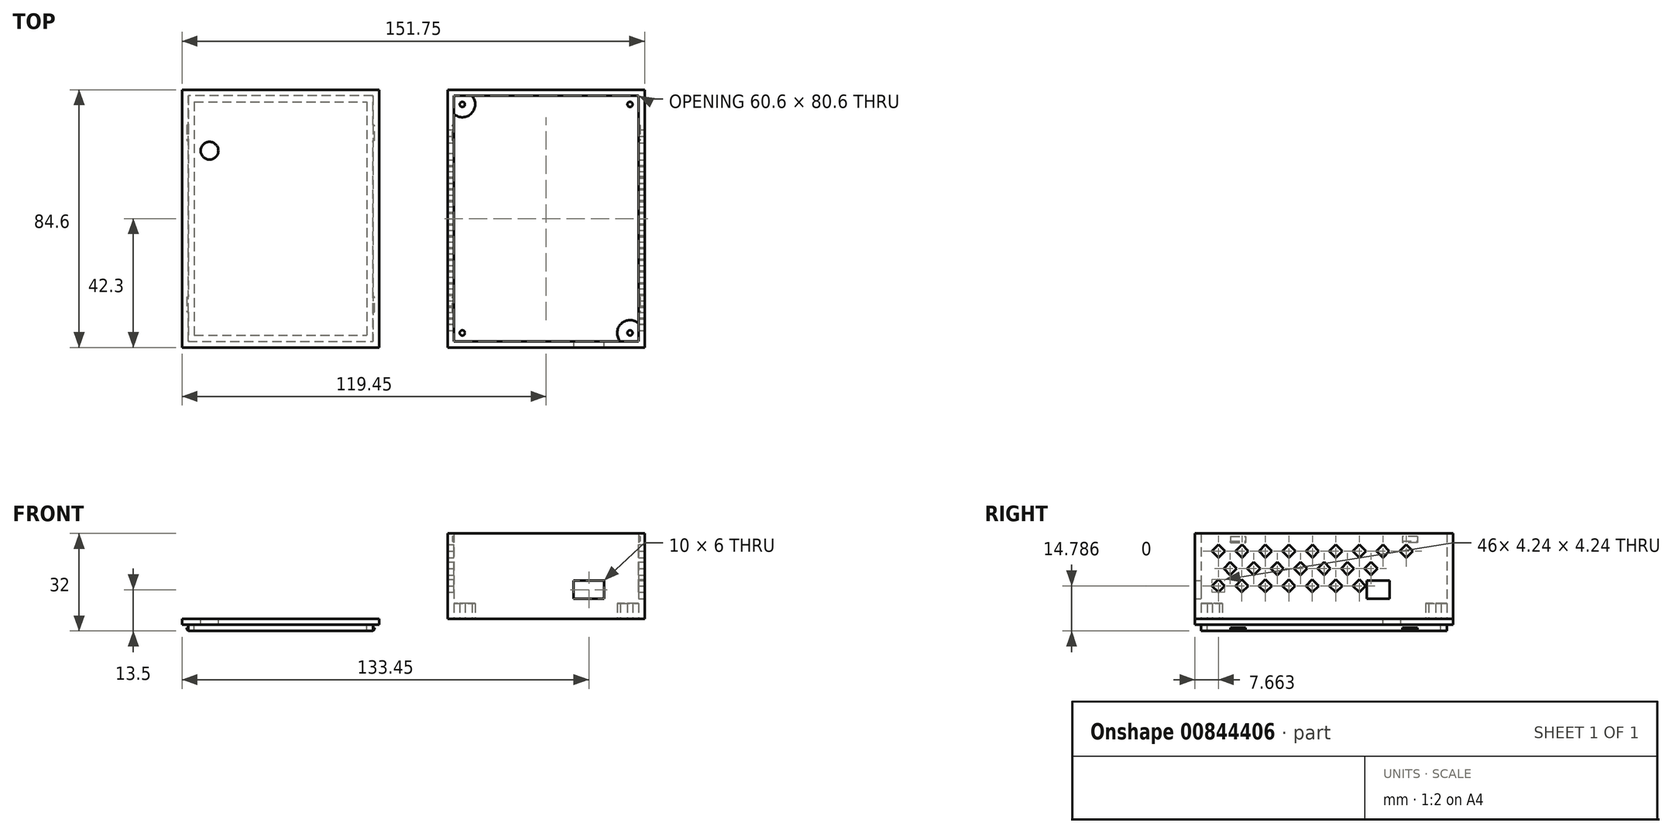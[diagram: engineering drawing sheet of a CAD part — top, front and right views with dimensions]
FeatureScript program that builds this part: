
annotation { "Feature Type Name" : "Feature", "Feature Type Description" : "" }
export const myFeature = defineFeature(function(context is Context, id is Id, definition is map)
    precondition{}
    {
        {
            var Q0;
            Q0=qCreatedBy(makeId("Top.planeOp"),FACE);
            var sketch = newSketch(context, id + "F0", { "sketchPlane" : qUnion([Q0])});
            skLineSegment(sketch, "E0", {"start": v(0, 47.12) * mm, "end": v(0, -56.68) * mm, "construction": true});
            skLineSegment(sketch, "E1", {"start": v(-53.86, 0) * mm, "end": v(97.7, 0) * mm, "construction": true});
            skCircle(sketch, "E2", {"center": v(-27.5, 37.5) * mm, "radius": 0.85 * mm});
            skLineSegment(sketch, "E3", {"start": v(-32.3, 0) * mm, "end": v(-32.3, 42.3) * mm});
            skLineSegment(sketch, "E4", {"start": v(-32.3, 42.3) * mm, "end": v(0, 42.3) * mm});
            skLineSegment(sketch, "E5", {"start": v(0, 40.3) * mm, "end": v(-30.3, 40.3) * mm});
            skLineSegment(sketch, "E6", {"start": v(-30.3, 40.3) * mm, "end": v(-30.3, 0) * mm});
            skCircle(sketch, "E7.MirrorC", {"center": v(27.5, 37.5) * mm, "radius": 0.85 * mm});
            skLineSegment(sketch, "E8.MirrorCS", {"start": v(32.3, 0) * mm, "end": v(32.3, 42.3) * mm});
            skLineSegment(sketch, "E9.MirrorCS", {"start": v(0, 40.3) * mm, "end": v(30.3, 40.3) * mm});
            skLineSegment(sketch, "E10.MirrorCS", {"start": v(30.3, 40.3) * mm, "end": v(30.3, 0) * mm});
            skLineSegment(sketch, "E11.MirrorCS", {"start": v(32.3, 42.3) * mm, "end": v(0, 42.3) * mm});
            skLineSegment(sketch, "E12.MirrorCS", {"start": v(-32.3, 0) * mm, "end": v(-32.3, -42.3) * mm});
            skLineSegment(sketch, "E13.MirrorCS", {"start": v(-30.3, -40.3) * mm, "end": v(-30.3, 0) * mm});
            skLineSegment(sketch, "E14.MirrorCS", {"start": v(30.3, -40.3) * mm, "end": v(30.3, 0) * mm});
            skLineSegment(sketch, "E15.MirrorCS", {"start": v(32.3, 0) * mm, "end": v(32.3, -42.3) * mm});
            skCircle(sketch, "E16.MirrorC", {"center": v(27.5, -37.5) * mm, "radius": 0.85 * mm});
            skCircle(sketch, "E17.MirrorC", {"center": v(-27.5, -37.5) * mm, "radius": 0.85 * mm});
            skLineSegment(sketch, "E18.MirrorCS", {"start": v(-32.3, -42.3) * mm, "end": v(0, -42.3) * mm});
            skLineSegment(sketch, "E19.MirrorCS", {"start": v(0, -40.3) * mm, "end": v(-30.3, -40.3) * mm});
            skLineSegment(sketch, "E20.MirrorCS", {"start": v(32.3, -42.3) * mm, "end": v(0, -42.3) * mm});
            skLineSegment(sketch, "E21.MirrorCS", {"start": v(0, -40.3) * mm, "end": v(30.3, -40.3) * mm});
            skLineSegment(sketch, "E22", {"start": v(30.3, 14) * mm, "end": v(32.3, 14) * mm});
            skLineSegment(sketch, "E23", {"start": v(30.3, 21.5) * mm, "end": v(32.3, 21.5) * mm});
            skLineSegment(sketch, "E24", {"start": v(19, -42.3) * mm, "end": v(19, -40.3) * mm});
            skLineSegment(sketch, "E25", {"start": v(9, -40.3) * mm, "end": v(9, -42.3) * mm});
            skArc(sketch, "E26", {"start": v(-24.36, 40.3) * mm, "mid": v(-24.53, 34.53) * mm, "end": v(-30.3, 34.36) * mm});
            skArc(sketch, "E27.MirrorCS", {"start": v(24.36, 40.3) * mm, "mid": v(24.53, 34.53) * mm, "end": v(30.3, 34.36) * mm});
            skArc(sketch, "E28.MirrorCS", {"start": v(24.36, -40.3) * mm, "mid": v(24.53, -34.53) * mm, "end": v(30.3, -34.36) * mm});
            skArc(sketch, "E29.MirrorCS", {"start": v(-24.36, -40.3) * mm, "mid": v(-24.53, -34.53) * mm, "end": v(-30.3, -34.36) * mm});
            skLineSegment(sketch, "E30", {"start": v(-30.3, 30.67) * mm, "end": v(-30.8, 30.67) * mm});
            skLineSegment(sketch, "E31", {"start": v(-30.8, 30.67) * mm, "end": v(-30.8, 25.67) * mm});
            skLineSegment(sketch, "E32", {"start": v(-30.8, 25.67) * mm, "end": v(-30.3, 25.67) * mm});
            skLineSegment(sketch, "E33.MirrorCS", {"start": v(30.8, 25.67) * mm, "end": v(30.3, 25.67) * mm});
            skLineSegment(sketch, "E34.MirrorCS", {"start": v(30.3, 30.67) * mm, "end": v(30.8, 30.67) * mm});
            skLineSegment(sketch, "E35.MirrorCS", {"start": v(30.8, 30.67) * mm, "end": v(30.8, 25.67) * mm});
            skLineSegment(sketch, "E36.MirrorCS", {"start": v(30.8, -25.67) * mm, "end": v(30.3, -25.67) * mm});
            skLineSegment(sketch, "E37.MirrorCS", {"start": v(30.3, -30.67) * mm, "end": v(30.8, -30.67) * mm});
            skLineSegment(sketch, "E38.MirrorCS", {"start": v(30.8, -30.67) * mm, "end": v(30.8, -25.67) * mm});
            skLineSegment(sketch, "E39.MirrorCS", {"start": v(-30.8, -25.67) * mm, "end": v(-30.3, -25.67) * mm});
            skLineSegment(sketch, "E40.MirrorCS", {"start": v(-30.8, -30.67) * mm, "end": v(-30.8, -25.67) * mm});
            skLineSegment(sketch, "E41.MirrorCS", {"start": v(-30.3, -30.67) * mm, "end": v(-30.8, -30.67) * mm});
            skLineSegment(sketch, "E42", {"start": v(-43.57, 67.12) * mm, "end": v(-43.57, -62.63) * mm, "construction": true});
            skLineSegment(sketch, "E43.MirrorCS", {"start": v(-56.85, 30.67) * mm, "end": v(-56.35, 30.67) * mm});
            skLineSegment(sketch, "E44.MirrorCS", {"start": v(-117.95, -25.67) * mm, "end": v(-117.45, -25.67) * mm});
            skLineSegment(sketch, "E45.MirrorCS", {"start": v(-117.45, -30.67) * mm, "end": v(-117.95, -30.67) * mm});
            skLineSegment(sketch, "E46.MirrorCS", {"start": v(-56.85, -30.67) * mm, "end": v(-56.35, -30.67) * mm});
            skLineSegment(sketch, "E47.MirrorCS", {"start": v(-117.95, 30.67) * mm, "end": v(-117.95, 25.67) * mm});
            skLineSegment(sketch, "E48.MirrorCS", {"start": v(-56.35, -25.67) * mm, "end": v(-56.85, -25.67) * mm});
            skLineSegment(sketch, "E49.MirrorCS", {"start": v(-117.45, 30.67) * mm, "end": v(-117.95, 30.67) * mm});
            skLineSegment(sketch, "E50.MirrorCS", {"start": v(-117.95, 25.67) * mm, "end": v(-117.45, 25.67) * mm});
            skLineSegment(sketch, "E51.MirrorCS", {"start": v(-56.35, 25.67) * mm, "end": v(-56.85, 25.67) * mm});
            skLineSegment(sketch, "E52.MirrorCS", {"start": v(-117.95, -30.67) * mm, "end": v(-117.95, -25.67) * mm});
            skLineSegment(sketch, "E53.MirrorCS", {"start": v(-56.35, 30.67) * mm, "end": v(-56.35, 25.67) * mm});
            skLineSegment(sketch, "E54.MirrorCS", {"start": v(-56.35, -30.67) * mm, "end": v(-56.35, -25.67) * mm});
            skLineSegment(sketch, "E55.MirrorCS", {"start": v(-119.45, 0) * mm, "end": v(-119.45, 42.3) * mm});
            skLineSegment(sketch, "E56.MirrorCS", {"start": v(-87.15, -40.3) * mm, "end": v(-56.85, -40.3) * mm});
            skLineSegment(sketch, "E57.MirrorCS", {"start": v(-117.45, 40.3) * mm, "end": v(-117.45, 0) * mm});
            skLineSegment(sketch, "E58.MirrorCS", {"start": v(-119.45, 0) * mm, "end": v(-119.45, -42.3) * mm});
            skLineSegment(sketch, "E59.MirrorCS", {"start": v(-87.15, 40.3) * mm, "end": v(-117.45, 40.3) * mm});
            skLineSegment(sketch, "E60.MirrorCS", {"start": v(-119.45, -42.3) * mm, "end": v(-87.15, -42.3) * mm});
            skLineSegment(sketch, "E61.MirrorCS", {"start": v(-54.85, 0) * mm, "end": v(-54.85, -42.3) * mm});
            skLineSegment(sketch, "E62.MirrorCS", {"start": v(-54.85, 42.3) * mm, "end": v(-87.15, 42.3) * mm});
            skLineSegment(sketch, "E63.MirrorCS", {"start": v(-56.85, 40.3) * mm, "end": v(-56.85, 0) * mm});
            skLineSegment(sketch, "E64.MirrorCS", {"start": v(-54.85, 0) * mm, "end": v(-54.85, 42.3) * mm});
            skLineSegment(sketch, "E65.MirrorCS", {"start": v(-56.85, -40.3) * mm, "end": v(-56.85, 0) * mm});
            skLineSegment(sketch, "E66.MirrorCS", {"start": v(-87.15, -40.3) * mm, "end": v(-117.45, -40.3) * mm});
            skLineSegment(sketch, "E67.MirrorCS", {"start": v(-87.15, 40.3) * mm, "end": v(-56.85, 40.3) * mm});
            skLineSegment(sketch, "E68.MirrorCS", {"start": v(-117.45, -40.3) * mm, "end": v(-117.45, 0) * mm});
            skLineSegment(sketch, "E69.MirrorCS", {"start": v(-54.85, -42.3) * mm, "end": v(-87.15, -42.3) * mm});
            skLineSegment(sketch, "E70.MirrorCS", {"start": v(-119.45, 42.3) * mm, "end": v(-87.15, 42.3) * mm});
            skLineSegment(sketch, "E71.bottom", {"start": v(-115.45, 38.3) * mm, "end": v(-58.85, 38.3) * mm});
            skLineSegment(sketch, "E71.top", {"start": v(-115.45, -38.3) * mm, "end": v(-58.85, -38.3) * mm});
            skLineSegment(sketch, "E71.left", {"start": v(-115.45, 38.3) * mm, "end": v(-115.45, -38.3) * mm});
            skLineSegment(sketch, "E71.right", {"start": v(-58.85, 38.3) * mm, "end": v(-58.85, -38.3) * mm});
            skCircle(sketch, "E72", {"center": v(-110.45, 22.3) * mm, "radius": 2.9 * mm});
            skSolve(sketch);
        }
        {
            var Q0;
            {var subQ7=sQuery(id+"F0.wireOp",EDGE,"E56.MirrorCS");Q0=makeQuery(id+"F0.imprint","IMPRINT",FACE,{"disambiguationData":[TD([[makeQuery(id+"F0.imprint","IMPRINT",EDGE,{"derivedFrom":subQ7}),1.0]])]});}
            extrude(context, id + "F1", {"entities" : qUnion([Q0]), "oppositeDirection" : true, "depth" : 4 * mm, "offsetDistance" : 25 * mm});
        }
        {
            var Q0;
            {var subQ1=sQuery(id+"F0.wireOp",EDGE,"E43.MirrorCS");Q0=makeQuery(id+"F0.imprint","IMPRINT",FACE,{"disambiguationData":[TD([[makeQuery(id+"F0.imprint","IMPRINT",EDGE,{"derivedFrom":subQ1}),1.0]])]});}
            var Q1;
            Q1=makeQuery(id+"F0.imprint","IMPRINT",FACE,{"disambiguationData":[TD([[makeQuery(id+"F0.imprint","IMPRINT",EDGE,{"derivedFrom":sQuery(id+"F0.wireOp",EDGE,"E71.bottom")}),-1.0]])]});
            var Q2;
            Q2=makeQuery(id+"F0.imprint","IMPRINT",FACE,{"disambiguationData":[TD([[makeQuery(id+"F0.imprint","IMPRINT",EDGE,{"derivedFrom":sQuery(id+"F0.wireOp",EDGE,"E47.MirrorCS")}),1.0]])]});
            var Q3;
            {var subQ0=sQuery(id+"F0.wireOp",EDGE,"E43.MirrorCS");Q3=makeQuery(id+"F0.imprint","IMPRINT",FACE,{"disambiguationData":[TD([[makeQuery(id+"F0.imprint","IMPRINT",EDGE,{"derivedFrom":subQ0}),-1.0]])]});}
            var Q4;
            {var subQ0=sQuery(id+"F0.wireOp",EDGE,"E46.MirrorCS");Q4=makeQuery(id+"F0.imprint","IMPRINT",FACE,{"disambiguationData":[TD([[makeQuery(id+"F0.imprint","IMPRINT",EDGE,{"derivedFrom":subQ0}),1.0]])]});}
            var Q5;
            {var subQ0=sQuery(id+"F0.wireOp",EDGE,"E44.MirrorCS");Q5=makeQuery(id+"F0.imprint","IMPRINT",FACE,{"disambiguationData":[TD([[makeQuery(id+"F0.imprint","IMPRINT",EDGE,{"derivedFrom":subQ0}),-1.0]])]});}
            extrude(context, id + "F2", {"entities" : qUnion([Q0, Q1, Q2, Q3, Q4, Q5]), "operationType" : NewBodyOperationType.ADD, "oppositeDirection" : true, "depth" : 2 * mm, "offsetDistance" : 25 * mm});
        }
        {
            var Q0;
            {var subQ0=sQuery(id+"F0.wireOp",EDGE,"E46.MirrorCS");Q0=makeQuery(id+"F0.imprint","IMPRINT",FACE,{"disambiguationData":[TD([[makeQuery(id+"F0.imprint","IMPRINT",EDGE,{"derivedFrom":subQ0}),1.0]])]});}
            var Q1;
            {var subQ0=sQuery(id+"F0.wireOp",EDGE,"E43.MirrorCS");Q1=makeQuery(id+"F0.imprint","IMPRINT",FACE,{"disambiguationData":[TD([[makeQuery(id+"F0.imprint","IMPRINT",EDGE,{"derivedFrom":subQ0}),-1.0]])]});}
            var Q2;
            Q2=makeQuery(id+"F0.imprint","IMPRINT",FACE,{"disambiguationData":[TD([[makeQuery(id+"F0.imprint","IMPRINT",EDGE,{"derivedFrom":sQuery(id+"F0.wireOp",EDGE,"E47.MirrorCS")}),1.0]])]});
            var Q3;
            {var subQ0=sQuery(id+"F0.wireOp",EDGE,"E44.MirrorCS");Q3=makeQuery(id+"F0.imprint","IMPRINT",FACE,{"disambiguationData":[TD([[makeQuery(id+"F0.imprint","IMPRINT",EDGE,{"derivedFrom":subQ0}),-1.0]])]});}
            extrude(context, id + "F3", {"entities" : qUnion([Q0, Q1, Q2, Q3]), "operationType" : NewBodyOperationType.ADD, "oppositeDirection" : true, "depth" : 4 * mm, "offsetDistance" : 25 * mm, "hasSecondDirection" : true, "secondDirectionOppositeDirection" : true, "secondDirectionDepth" : 3 * mm});
        }
        {
            var Q0;
            Q0=makeQuery(id+"F0.imprint","IMPRINT",FACE,{"disambiguationData":[TD([[makeQuery(id+"F0.imprint","IMPRINT",EDGE,{"derivedFrom":sQuery(id+"F0.wireOp",EDGE,"E2")}),-1.0]])]});
            var Q1;
            Q1=makeQuery(id+"F0.imprint","IMPRINT",FACE,{"disambiguationData":[TD([[makeQuery(id+"F0.imprint","IMPRINT",EDGE,{"derivedFrom":sQuery(id+"F0.wireOp",EDGE,"E7.MirrorC")}),1.0]])]});
            var Q2;
            Q2=makeQuery(id+"F0.imprint","IMPRINT",FACE,{"disambiguationData":[TD([[makeQuery(id+"F0.imprint","IMPRINT",EDGE,{"derivedFrom":sQuery(id+"F0.wireOp",EDGE,"E16.MirrorC")}),-1.0]])]});
            var Q3;
            Q3=makeQuery(id+"F0.imprint","IMPRINT",FACE,{"disambiguationData":[TD([[makeQuery(id+"F0.imprint","IMPRINT",EDGE,{"derivedFrom":sQuery(id+"F0.wireOp",EDGE,"E17.MirrorC")}),1.0]])]});
            extrude(context, id + "F4", {"entities" : qUnion([Q0, Q1, Q2, Q3]), "depth" : 5 * mm, "offsetDistance" : 25 * mm});
        }
        {
            var Q0;
            {var subQ7=sQuery(id+"F0.wireOp",EDGE,"E26");Q0=makeQuery(id+"F0.imprint","IMPRINT",FACE,{"disambiguationData":[TD([[makeQuery(id+"F0.imprint","IMPRINT",EDGE,{"derivedFrom":subQ7}),1.0]])]});}
            extrude(context, id + "F5", {"entities" : qUnion([Q0]), "operationType" : NewBodyOperationType.ADD, "depth" : 2 * mm, "offsetDistance" : 25 * mm});
        }
        {
            var Q0;
            {var subQ0=sQuery(id+"F0.wireOp",EDGE,"E36.MirrorCS");Q0=makeQuery(id+"F0.imprint","IMPRINT",FACE,{"disambiguationData":[TD([[makeQuery(id+"F0.imprint","IMPRINT",EDGE,{"derivedFrom":subQ0}),1.0]])]});}
            var Q1;
            {var subQ2=sQuery(id+"F0.wireOp",EDGE,"E15.MirrorCS");Q1=makeQuery(id+"F0.imprint","IMPRINT",FACE,{"disambiguationData":[TD([[makeQuery(id+"F0.imprint","IMPRINT",EDGE,{"derivedFrom":subQ2}),-1.0]])]});}
            var Q2;
            {var subQ0=sQuery(id+"F0.wireOp",EDGE,"E24");Q2=makeQuery(id+"F0.imprint","IMPRINT",FACE,{"disambiguationData":[TD([[makeQuery(id+"F0.imprint","IMPRINT",EDGE,{"derivedFrom":subQ0}),1.0]])]});}
            var Q3;
            Q3=makeQuery(id+"F0.imprint","IMPRINT",FACE,{"disambiguationData":[TD([[makeQuery(id+"F0.imprint","IMPRINT",EDGE,{"derivedFrom":sQuery(id+"F0.wireOp",EDGE,"E3")}),-1.0]])]});
            var Q4;
            {var subQ0=sQuery(id+"F0.wireOp",EDGE,"E22");Q4=makeQuery(id+"F0.imprint","IMPRINT",FACE,{"disambiguationData":[TD([[makeQuery(id+"F0.imprint","IMPRINT",EDGE,{"derivedFrom":subQ0}),1.0]])]});}
            var Q5;
            {var subQ0=sQuery(id+"F0.wireOp",EDGE,"E33.MirrorCS");Q5=makeQuery(id+"F0.imprint","IMPRINT",FACE,{"disambiguationData":[TD([[makeQuery(id+"F0.imprint","IMPRINT",EDGE,{"derivedFrom":subQ0}),-1.0]])]});}
            var Q6;
            {var subQ0=sQuery(id+"F0.wireOp",EDGE,"E39.MirrorCS");Q6=makeQuery(id+"F0.imprint","IMPRINT",FACE,{"disambiguationData":[TD([[makeQuery(id+"F0.imprint","IMPRINT",EDGE,{"derivedFrom":subQ0}),-1.0]])]});}
            var Q7;
            {var subQ0=sQuery(id+"F0.wireOp",EDGE,"E30");Q7=makeQuery(id+"F0.imprint","IMPRINT",FACE,{"disambiguationData":[TD([[makeQuery(id+"F0.imprint","IMPRINT",EDGE,{"derivedFrom":subQ0}),1.0]])]});}
            extrude(context, id + "F6", {"entities" : qUnion([Q0, Q1, Q2, Q3, Q4, Q5, Q6, Q7]), "operationType" : NewBodyOperationType.ADD, "depth" : 28 * mm, "offsetDistance" : 25 * mm});
        }
        {
            var Q0;
            {var subQ0=sQuery(id+"F0.wireOp",EDGE,"E30");Q0=makeQuery(id+"F0.imprint","IMPRINT",FACE,{"disambiguationData":[TD([[makeQuery(id+"F0.imprint","IMPRINT",EDGE,{"derivedFrom":subQ0}),1.0]])]});}
            var Q1;
            {var subQ0=sQuery(id+"F0.wireOp",EDGE,"E39.MirrorCS");Q1=makeQuery(id+"F0.imprint","IMPRINT",FACE,{"disambiguationData":[TD([[makeQuery(id+"F0.imprint","IMPRINT",EDGE,{"derivedFrom":subQ0}),-1.0]])]});}
            var Q2;
            {var subQ0=sQuery(id+"F0.wireOp",EDGE,"E36.MirrorCS");Q2=makeQuery(id+"F0.imprint","IMPRINT",FACE,{"disambiguationData":[TD([[makeQuery(id+"F0.imprint","IMPRINT",EDGE,{"derivedFrom":subQ0}),1.0]])]});}
            var Q3;
            {var subQ0=sQuery(id+"F0.wireOp",EDGE,"E33.MirrorCS");Q3=makeQuery(id+"F0.imprint","IMPRINT",FACE,{"disambiguationData":[TD([[makeQuery(id+"F0.imprint","IMPRINT",EDGE,{"derivedFrom":subQ0}),-1.0]])]});}
            extrude(context, id + "F7", {"entities" : qUnion([Q0, Q1, Q2, Q3]), "operationType" : NewBodyOperationType.REMOVE, "depth" : 27 * mm, "offsetDistance" : 25 * mm, "hasSecondDirection" : true, "secondDirectionOppositeDirection" : false, "secondDirectionDepth" : 25 * mm});
        }
        {
            var Q0;
            Q0=makeQuery(id+"F7.boolean.opBoolean","COPY",EDGE,{"derivedFrom":makeQuery(id+"F7.opExtrude","CAP_EDGE",EDGE,{"disambiguationData":[OSD([sQuery(id+"F0.wireOp",EDGE,"E31")])],"isStart":true})});
            var Q1;
            Q1=makeQuery(id+"F7.boolean.opBoolean","COPY",EDGE,{"derivedFrom":makeQuery(id+"F7.opExtrude","CAP_EDGE",EDGE,{"disambiguationData":[OSD([sQuery(id+"F0.wireOp",EDGE,"E6")])],"isStart":false})});
            var Q2;
            Q2=makeQuery(id+"F7.boolean.opBoolean","COPY",EDGE,{"derivedFrom":makeQuery(id+"F7.opExtrude","CAP_EDGE",EDGE,{"disambiguationData":[OSD([sQuery(id+"F0.wireOp",EDGE,"E13.MirrorCS")])],"isStart":false})});
            var Q3;
            Q3=makeQuery(id+"F7.boolean.opBoolean","COPY",EDGE,{"derivedFrom":makeQuery(id+"F7.opExtrude","CAP_EDGE",EDGE,{"disambiguationData":[OSD([sQuery(id+"F0.wireOp",EDGE,"E40.MirrorCS")])],"isStart":true})});
            var Q4;
            Q4=makeQuery(id+"F7.boolean.opBoolean","COPY",EDGE,{"derivedFrom":makeQuery(id+"F7.opExtrude","CAP_EDGE",EDGE,{"disambiguationData":[OSD([sQuery(id+"F0.wireOp",EDGE,"E10.MirrorCS")])],"isStart":false})});
            var Q5;
            Q5=makeQuery(id+"F7.boolean.opBoolean","COPY",EDGE,{"derivedFrom":makeQuery(id+"F7.opExtrude","CAP_EDGE",EDGE,{"disambiguationData":[OSD([sQuery(id+"F0.wireOp",EDGE,"E35.MirrorCS")])],"isStart":true})});
            var Q6;
            Q6=makeQuery(id+"F7.boolean.opBoolean","COPY",EDGE,{"derivedFrom":makeQuery(id+"F7.opExtrude","CAP_EDGE",EDGE,{"disambiguationData":[OSD([sQuery(id+"F0.wireOp",EDGE,"E14.MirrorCS")])],"isStart":false})});
            var Q7;
            Q7=makeQuery(id+"F7.boolean.opBoolean","COPY",EDGE,{"derivedFrom":makeQuery(id+"F7.opExtrude","CAP_EDGE",EDGE,{"disambiguationData":[OSD([sQuery(id+"F0.wireOp",EDGE,"E38.MirrorCS")])],"isStart":true})});
            var Q8;
            Q8=makeQuery(id+"F3.opExtrude","CAP_EDGE",EDGE,{"disambiguationData":[OSD([sQuery(id+"F0.wireOp",EDGE,"E68.MirrorCS")])],"isStart":true});
            var Q9;
            Q9=makeQuery(id+"F3.opExtrude","CAP_EDGE",EDGE,{"disambiguationData":[OSD([sQuery(id+"F0.wireOp",EDGE,"E52.MirrorCS")])],"isStart":false});
            var Q10;
            Q10=makeQuery(id+"F3.opExtrude","CAP_EDGE",EDGE,{"disambiguationData":[OSD([sQuery(id+"F0.wireOp",EDGE,"E47.MirrorCS")])],"isStart":false});
            var Q11;
            Q11=makeQuery(id+"F3.opExtrude","CAP_EDGE",EDGE,{"disambiguationData":[OSD([sQuery(id+"F0.wireOp",EDGE,"E57.MirrorCS")])],"isStart":true});
            var Q12;
            Q12=makeQuery(id+"F3.opExtrude","CAP_EDGE",EDGE,{"disambiguationData":[OSD([sQuery(id+"F0.wireOp",EDGE,"E53.MirrorCS")])],"isStart":false});
            var Q13;
            Q13=makeQuery(id+"F3.opExtrude","CAP_EDGE",EDGE,{"disambiguationData":[OSD([sQuery(id+"F0.wireOp",EDGE,"E63.MirrorCS")])],"isStart":true});
            var Q14;
            Q14=makeQuery(id+"F3.opExtrude","CAP_EDGE",EDGE,{"disambiguationData":[OSD([sQuery(id+"F0.wireOp",EDGE,"E65.MirrorCS")])],"isStart":true});
            var Q15;
            Q15=makeQuery(id+"F3.opExtrude","CAP_EDGE",EDGE,{"disambiguationData":[OSD([sQuery(id+"F0.wireOp",EDGE,"E54.MirrorCS")])],"isStart":false});
            chamfer(context, id + "F8", {"entities" : qUnion([Q0, Q1, Q2, Q3, Q4, Q5, Q6, Q7, Q8, Q9, Q10, Q11, Q12, Q13, Q14, Q15]), "width" : 0.5 * mm, "tangentPropagation" : true});
        }
        {
            var Q0;
            {var subQ0=sQuery(id+"F0.wireOp",EDGE,"E24");Q0=makeQuery(id+"F0.imprint","IMPRINT",FACE,{"disambiguationData":[TD([[makeQuery(id+"F0.imprint","IMPRINT",EDGE,{"derivedFrom":subQ0}),1.0]])]});}
            var Q1;
            {var subQ0=sQuery(id+"F0.wireOp",EDGE,"E22");Q1=makeQuery(id+"F0.imprint","IMPRINT",FACE,{"disambiguationData":[TD([[makeQuery(id+"F0.imprint","IMPRINT",EDGE,{"derivedFrom":subQ0}),1.0]])]});}
            extrude(context, id + "F9", {"entities" : qUnion([Q0, Q1]), "operationType" : NewBodyOperationType.REMOVE, "depth" : 12.5 * mm, "offsetDistance" : 25 * mm, "hasSecondDirection" : true, "secondDirectionOppositeDirection" : false, "secondDirectionDepth" : 6.5 * mm});
        }
        {
            var Q0;
            Q0=makeQuery(id+"F6.opExtrude","SWEPT_FACE",FACE,{"disambiguationData":[OSD([sQuery(id+"F0.wireOp",EDGE,"E8.MirrorCS"),sQuery(id+"F0.wireOp",EDGE,"E15.MirrorCS")])]});
            var sketch = newSketch(context, id + "F10", { "sketchPlane" : qUnion([Q0])});
            skLineSegment(sketch, "E73.bottom", {"start": v(-42.3, 24.3) * mm, "end": v(-44.42, 22.19) * mm});
            skLineSegment(sketch, "E73.top", {"start": v(-40.18, 22.19) * mm, "end": v(-42.3, 20.07) * mm});
            skLineSegment(sketch, "E73.left", {"start": v(-42.3, 24.3) * mm, "end": v(-40.18, 22.19) * mm});
            skLineSegment(sketch, "E73.right", {"start": v(-44.42, 22.19) * mm, "end": v(-42.3, 20.07) * mm});
            skPoint(sketch, "E73.middle", {"position": v(-42.3, 22.19) * mm});
            skPoint(sketch, "E74.1.0.0", {"position": v(-34.6, 22.19) * mm});
            skLineSegment(sketch, "E74.1.0.1", {"start": v(-32.48, 22.19) * mm, "end": v(-34.6, 20.07) * mm});
            skLineSegment(sketch, "E74.1.0.2", {"start": v(-34.6, 24.3) * mm, "end": v(-32.48, 22.19) * mm});
            skLineSegment(sketch, "E74.1.0.3", {"start": v(-34.6, 24.3) * mm, "end": v(-36.72, 22.19) * mm});
            skLineSegment(sketch, "E74.1.0.4", {"start": v(-36.72, 22.19) * mm, "end": v(-34.6, 20.07) * mm});
            skPoint(sketch, "E74.2.0.0", {"position": v(-26.9, 22.19) * mm});
            skLineSegment(sketch, "E74.2.0.1", {"start": v(-24.78, 22.19) * mm, "end": v(-26.9, 20.07) * mm});
            skLineSegment(sketch, "E74.2.0.2", {"start": v(-26.9, 24.3) * mm, "end": v(-24.78, 22.19) * mm});
            skLineSegment(sketch, "E74.2.0.3", {"start": v(-26.9, 24.3) * mm, "end": v(-29.02, 22.19) * mm});
            skLineSegment(sketch, "E74.2.0.4", {"start": v(-29.02, 22.19) * mm, "end": v(-26.9, 20.07) * mm});
            skPoint(sketch, "E74.3.0.0", {"position": v(-19.2, 22.19) * mm});
            skLineSegment(sketch, "E74.3.0.1", {"start": v(-17.08, 22.19) * mm, "end": v(-19.2, 20.07) * mm});
            skLineSegment(sketch, "E74.3.0.2", {"start": v(-19.2, 24.3) * mm, "end": v(-17.08, 22.19) * mm});
            skLineSegment(sketch, "E74.3.0.3", {"start": v(-19.2, 24.3) * mm, "end": v(-21.32, 22.19) * mm});
            skLineSegment(sketch, "E74.3.0.4", {"start": v(-21.32, 22.19) * mm, "end": v(-19.2, 20.07) * mm});
            skPoint(sketch, "E74.4.0.0", {"position": v(-11.5, 22.19) * mm});
            skLineSegment(sketch, "E74.4.0.1", {"start": v(-9.38, 22.19) * mm, "end": v(-11.5, 20.07) * mm});
            skLineSegment(sketch, "E74.4.0.2", {"start": v(-11.5, 24.3) * mm, "end": v(-9.38, 22.19) * mm});
            skLineSegment(sketch, "E74.4.0.3", {"start": v(-11.5, 24.3) * mm, "end": v(-13.62, 22.19) * mm});
            skLineSegment(sketch, "E74.4.0.4", {"start": v(-13.62, 22.19) * mm, "end": v(-11.5, 20.07) * mm});
            skPoint(sketch, "E74.5.0.0", {"position": v(-3.8, 22.19) * mm});
            skLineSegment(sketch, "E74.5.0.1", {"start": v(-1.68, 22.19) * mm, "end": v(-3.8, 20.07) * mm});
            skLineSegment(sketch, "E74.5.0.2", {"start": v(-3.8, 24.3) * mm, "end": v(-1.68, 22.19) * mm});
            skLineSegment(sketch, "E74.5.0.3", {"start": v(-3.8, 24.3) * mm, "end": v(-5.92, 22.19) * mm});
            skLineSegment(sketch, "E74.5.0.4", {"start": v(-5.92, 22.19) * mm, "end": v(-3.8, 20.07) * mm});
            skPoint(sketch, "E74.6.0.0", {"position": v(3.9, 22.19) * mm});
            skLineSegment(sketch, "E74.6.0.1", {"start": v(6.02, 22.19) * mm, "end": v(3.9, 20.07) * mm});
            skLineSegment(sketch, "E74.6.0.2", {"start": v(3.9, 24.3) * mm, "end": v(6.02, 22.19) * mm});
            skLineSegment(sketch, "E74.6.0.3", {"start": v(3.9, 24.3) * mm, "end": v(1.78, 22.19) * mm});
            skLineSegment(sketch, "E74.6.0.4", {"start": v(1.78, 22.19) * mm, "end": v(3.9, 20.07) * mm});
            skPoint(sketch, "E74.7.0.0", {"position": v(11.6, 22.19) * mm});
            skLineSegment(sketch, "E74.7.0.1", {"start": v(13.72, 22.19) * mm, "end": v(11.6, 20.07) * mm});
            skLineSegment(sketch, "E74.7.0.2", {"start": v(11.6, 24.3) * mm, "end": v(13.72, 22.19) * mm});
            skLineSegment(sketch, "E74.7.0.3", {"start": v(11.6, 24.3) * mm, "end": v(9.48, 22.19) * mm});
            skLineSegment(sketch, "E74.7.0.4", {"start": v(9.48, 22.19) * mm, "end": v(11.6, 20.07) * mm});
            skPoint(sketch, "E74.8.0.0", {"position": v(19.3, 22.19) * mm});
            skLineSegment(sketch, "E74.8.0.1", {"start": v(21.42, 22.19) * mm, "end": v(19.3, 20.07) * mm});
            skLineSegment(sketch, "E74.8.0.2", {"start": v(19.3, 24.3) * mm, "end": v(21.42, 22.19) * mm});
            skLineSegment(sketch, "E74.8.0.3", {"start": v(19.3, 24.3) * mm, "end": v(17.18, 22.19) * mm});
            skLineSegment(sketch, "E74.8.0.4", {"start": v(17.18, 22.19) * mm, "end": v(19.3, 20.07) * mm});
            skPoint(sketch, "E74.9.0.0", {"position": v(27, 22.19) * mm});
            skLineSegment(sketch, "E74.9.0.1", {"start": v(29.12, 22.19) * mm, "end": v(27, 20.07) * mm});
            skLineSegment(sketch, "E74.9.0.2", {"start": v(27, 24.3) * mm, "end": v(29.12, 22.19) * mm});
            skLineSegment(sketch, "E74.9.0.3", {"start": v(27, 24.3) * mm, "end": v(24.88, 22.19) * mm});
            skLineSegment(sketch, "E74.9.0.4", {"start": v(24.88, 22.19) * mm, "end": v(27, 20.07) * mm});
            skLineSegment(sketch, "E74.direction1", {"start": v(-42.3, 20.07) * mm, "end": v(-34.6, 20.07) * mm, "construction": true});
            skLineSegment(sketch, "E75", {"start": v(-44.4, 13.75) * mm, "end": v(52.6, 13.75) * mm, "construction": true});
            skLineSegment(sketch, "E76.direction1", {"start": v(-36.83, 19.94) * mm, "end": v(-36.83, 13.94) * mm, "construction": true});
            skPoint(sketch, "E77.1.0.0", {"position": v(-23.07, 16.49) * mm});
            skLineSegment(sketch, "E77.1.0.1", {"start": v(-17.49, 16.49) * mm, "end": v(-15.37, 14.37) * mm});
            skLineSegment(sketch, "E77.1.0.2", {"start": v(17.55, 16.49) * mm, "end": v(15.43, 14.37) * mm});
            skPoint(sketch, "E77.1.0.3", {"position": v(-7.67, 16.49) * mm});
            skLineSegment(sketch, "E77.1.0.4", {"start": v(25.25, 16.49) * mm, "end": v(23.13, 14.37) * mm});
            skLineSegment(sketch, "E77.1.0.5", {"start": v(-23.07, 18.6) * mm, "end": v(-25.19, 16.49) * mm});
            skPoint(sketch, "E77.1.0.6", {"position": v(-30.77, 16.49) * mm});
            skPoint(sketch, "E77.1.0.7", {"position": v(23.13, 16.49) * mm});
            skPoint(sketch, "E77.1.0.8", {"position": v(15.43, 16.49) * mm});
            skLineSegment(sketch, "E77.1.0.9", {"start": v(28.71, 16.49) * mm, "end": v(30.83, 14.37) * mm});
            skLineSegment(sketch, "E77.1.0.10", {"start": v(5.61, 16.49) * mm, "end": v(7.73, 14.37) * mm});
            skLineSegment(sketch, "E77.1.0.11", {"start": v(9.85, 16.49) * mm, "end": v(7.73, 14.37) * mm});
            skPoint(sketch, "E77.1.0.12", {"position": v(-38.47, 16.49) * mm});
            skLineSegment(sketch, "E77.1.0.13", {"start": v(13.31, 16.49) * mm, "end": v(15.43, 14.37) * mm});
            skLineSegment(sketch, "E77.1.0.14", {"start": v(21.01, 16.49) * mm, "end": v(23.13, 14.37) * mm});
            skLineSegment(sketch, "E77.1.0.15", {"start": v(-32.89, 16.49) * mm, "end": v(-30.77, 14.37) * mm});
            skLineSegment(sketch, "E77.1.0.16", {"start": v(-9.79, 16.49) * mm, "end": v(-7.67, 14.37) * mm});
            skPoint(sketch, "E77.1.0.17", {"position": v(-15.37, 16.49) * mm});
            skPoint(sketch, "E77.1.0.18", {"position": v(7.73, 16.49) * mm});
            skLineSegment(sketch, "E77.1.0.19", {"start": v(-2.09, 16.49) * mm, "end": v(0.03, 14.37) * mm});
            skLineSegment(sketch, "E77.1.0.20", {"start": v(-15.37, 18.6) * mm, "end": v(-17.49, 16.49) * mm});
            skPoint(sketch, "E77.1.0.21", {"position": v(0.03, 16.49) * mm});
            skPoint(sketch, "E77.1.0.22", {"position": v(30.83, 16.49) * mm});
            skLineSegment(sketch, "E77.1.0.23", {"start": v(-25.19, 16.49) * mm, "end": v(-23.07, 14.37) * mm});
            skLineSegment(sketch, "E77.1.0.24", {"start": v(2.15, 16.49) * mm, "end": v(0.03, 14.37) * mm});
            skLineSegment(sketch, "E77.1.0.25", {"start": v(-5.55, 16.49) * mm, "end": v(-7.67, 14.37) * mm});
            skLineSegment(sketch, "E77.1.0.26", {"start": v(-38.47, 14.37) * mm, "end": v(-30.77, 14.37) * mm, "construction": true});
            skLineSegment(sketch, "E77.1.0.27", {"start": v(-13.25, 16.49) * mm, "end": v(-15.37, 14.37) * mm});
            skLineSegment(sketch, "E77.1.0.28", {"start": v(-38.47, 18.6) * mm, "end": v(-36.35, 16.49) * mm});
            skLineSegment(sketch, "E77.1.0.29", {"start": v(32.95, 16.49) * mm, "end": v(30.83, 14.37) * mm});
            skLineSegment(sketch, "E77.1.0.30", {"start": v(-7.67, 18.6) * mm, "end": v(-9.79, 16.49) * mm});
            skLineSegment(sketch, "E77.1.0.31", {"start": v(-30.77, 18.6) * mm, "end": v(-32.89, 16.49) * mm});
            skLineSegment(sketch, "E77.1.0.32", {"start": v(-36.35, 16.49) * mm, "end": v(-38.47, 14.37) * mm});
            skLineSegment(sketch, "E77.1.0.33", {"start": v(-20.95, 16.49) * mm, "end": v(-23.07, 14.37) * mm});
            skLineSegment(sketch, "E77.1.0.34", {"start": v(30.83, 18.6) * mm, "end": v(28.71, 16.49) * mm});
            skLineSegment(sketch, "E77.1.0.35", {"start": v(-38.47, 18.6) * mm, "end": v(-40.59, 16.49) * mm});
            skLineSegment(sketch, "E77.1.0.36", {"start": v(0.03, 18.6) * mm, "end": v(-2.09, 16.49) * mm});
            skLineSegment(sketch, "E77.1.0.37", {"start": v(15.43, 18.6) * mm, "end": v(13.31, 16.49) * mm});
            skLineSegment(sketch, "E77.1.0.38", {"start": v(15.43, 18.6) * mm, "end": v(17.55, 16.49) * mm});
            skLineSegment(sketch, "E77.1.0.39", {"start": v(-15.37, 18.6) * mm, "end": v(-13.25, 16.49) * mm});
            skLineSegment(sketch, "E77.1.0.40", {"start": v(-30.77, 18.6) * mm, "end": v(-28.65, 16.49) * mm});
            skLineSegment(sketch, "E77.1.0.41", {"start": v(7.73, 18.6) * mm, "end": v(9.85, 16.49) * mm});
            skLineSegment(sketch, "E77.1.0.42", {"start": v(23.13, 18.6) * mm, "end": v(25.25, 16.49) * mm});
            skLineSegment(sketch, "E77.1.0.43", {"start": v(30.83, 18.6) * mm, "end": v(32.95, 16.49) * mm});
            skLineSegment(sketch, "E77.1.0.44", {"start": v(-40.59, 16.49) * mm, "end": v(-38.47, 14.37) * mm});
            skLineSegment(sketch, "E77.1.0.45", {"start": v(-23.07, 18.6) * mm, "end": v(-20.95, 16.49) * mm});
            skLineSegment(sketch, "E77.1.0.46", {"start": v(-28.65, 16.49) * mm, "end": v(-30.77, 14.37) * mm});
            skLineSegment(sketch, "E77.1.0.47", {"start": v(7.73, 18.6) * mm, "end": v(5.61, 16.49) * mm});
            skLineSegment(sketch, "E77.1.0.48", {"start": v(-7.67, 18.6) * mm, "end": v(-5.55, 16.49) * mm});
            skLineSegment(sketch, "E77.1.0.49", {"start": v(23.13, 18.6) * mm, "end": v(21.01, 16.49) * mm});
            skLineSegment(sketch, "E77.1.0.50", {"start": v(0.03, 18.6) * mm, "end": v(2.15, 16.49) * mm});
            skPoint(sketch, "E77.2.0.0", {"position": v(-19.24, 10.79) * mm});
            skLineSegment(sketch, "E77.2.0.1", {"start": v(-13.66, 10.79) * mm, "end": v(-11.54, 8.66) * mm});
            skLineSegment(sketch, "E77.2.0.2", {"start": v(21.38, 10.79) * mm, "end": v(19.26, 8.66) * mm});
            skPoint(sketch, "E77.2.0.3", {"position": v(-3.84, 10.79) * mm});
            skLineSegment(sketch, "E77.2.0.4", {"start": v(29.08, 10.79) * mm, "end": v(26.96, 8.66) * mm});
            skLineSegment(sketch, "E77.2.0.5", {"start": v(-19.24, 12.9) * mm, "end": v(-21.36, 10.79) * mm});
            skPoint(sketch, "E77.2.0.6", {"position": v(-26.94, 10.79) * mm});
            skPoint(sketch, "E77.2.0.7", {"position": v(26.96, 10.79) * mm});
            skPoint(sketch, "E77.2.0.8", {"position": v(19.26, 10.79) * mm});
            skLineSegment(sketch, "E77.2.0.9", {"start": v(32.54, 10.79) * mm, "end": v(34.66, 8.66) * mm});
            skLineSegment(sketch, "E77.2.0.10", {"start": v(9.44, 10.79) * mm, "end": v(11.56, 8.66) * mm});
            skLineSegment(sketch, "E77.2.0.11", {"start": v(13.68, 10.79) * mm, "end": v(11.56, 8.66) * mm});
            skPoint(sketch, "E77.2.0.12", {"position": v(-34.64, 10.79) * mm});
            skLineSegment(sketch, "E77.2.0.13", {"start": v(17.14, 10.79) * mm, "end": v(19.26, 8.66) * mm});
            skLineSegment(sketch, "E77.2.0.14", {"start": v(24.84, 10.79) * mm, "end": v(26.96, 8.66) * mm});
            skLineSegment(sketch, "E77.2.0.15", {"start": v(-29.06, 10.79) * mm, "end": v(-26.94, 8.66) * mm});
            skLineSegment(sketch, "E77.2.0.16", {"start": v(-5.96, 10.79) * mm, "end": v(-3.84, 8.66) * mm});
            skPoint(sketch, "E77.2.0.17", {"position": v(-11.54, 10.79) * mm});
            skPoint(sketch, "E77.2.0.18", {"position": v(11.56, 10.79) * mm});
            skLineSegment(sketch, "E77.2.0.19", {"start": v(1.74, 10.79) * mm, "end": v(3.86, 8.66) * mm});
            skLineSegment(sketch, "E77.2.0.20", {"start": v(-11.54, 12.9) * mm, "end": v(-13.66, 10.79) * mm});
            skPoint(sketch, "E77.2.0.21", {"position": v(3.86, 10.79) * mm});
            skPoint(sketch, "E77.2.0.22", {"position": v(34.66, 10.79) * mm});
            skLineSegment(sketch, "E77.2.0.23", {"start": v(-21.36, 10.79) * mm, "end": v(-19.24, 8.66) * mm});
            skLineSegment(sketch, "E77.2.0.24", {"start": v(5.98, 10.79) * mm, "end": v(3.86, 8.66) * mm});
            skLineSegment(sketch, "E77.2.0.25", {"start": v(-1.72, 10.79) * mm, "end": v(-3.84, 8.66) * mm});
            skLineSegment(sketch, "E77.2.0.26", {"start": v(-34.64, 8.66) * mm, "end": v(-26.94, 8.66) * mm, "construction": true});
            skLineSegment(sketch, "E77.2.0.27", {"start": v(-9.42, 10.79) * mm, "end": v(-11.54, 8.66) * mm});
            skLineSegment(sketch, "E77.2.0.28", {"start": v(-34.64, 12.9) * mm, "end": v(-32.52, 10.79) * mm});
            skLineSegment(sketch, "E77.2.0.29", {"start": v(36.78, 10.79) * mm, "end": v(34.66, 8.66) * mm});
            skLineSegment(sketch, "E77.2.0.30", {"start": v(-3.84, 12.9) * mm, "end": v(-5.96, 10.79) * mm});
            skLineSegment(sketch, "E77.2.0.31", {"start": v(-26.94, 12.9) * mm, "end": v(-29.06, 10.79) * mm});
            skLineSegment(sketch, "E77.2.0.32", {"start": v(-32.52, 10.79) * mm, "end": v(-34.64, 8.66) * mm});
            skLineSegment(sketch, "E77.2.0.33", {"start": v(-17.12, 10.79) * mm, "end": v(-19.24, 8.66) * mm});
            skLineSegment(sketch, "E77.2.0.34", {"start": v(34.66, 12.9) * mm, "end": v(32.54, 10.79) * mm});
            skLineSegment(sketch, "E77.2.0.35", {"start": v(-34.64, 12.9) * mm, "end": v(-36.76, 10.79) * mm});
            skLineSegment(sketch, "E77.2.0.36", {"start": v(3.86, 12.9) * mm, "end": v(1.74, 10.79) * mm});
            skLineSegment(sketch, "E77.2.0.37", {"start": v(19.26, 12.9) * mm, "end": v(17.14, 10.79) * mm});
            skLineSegment(sketch, "E77.2.0.38", {"start": v(19.26, 12.9) * mm, "end": v(21.38, 10.79) * mm});
            skLineSegment(sketch, "E77.2.0.39", {"start": v(-11.54, 12.9) * mm, "end": v(-9.42, 10.79) * mm});
            skLineSegment(sketch, "E77.2.0.40", {"start": v(-26.94, 12.9) * mm, "end": v(-24.82, 10.79) * mm});
            skLineSegment(sketch, "E77.2.0.41", {"start": v(11.56, 12.9) * mm, "end": v(13.68, 10.79) * mm});
            skLineSegment(sketch, "E77.2.0.42", {"start": v(26.96, 12.9) * mm, "end": v(29.08, 10.79) * mm});
            skLineSegment(sketch, "E77.2.0.43", {"start": v(34.66, 12.9) * mm, "end": v(36.78, 10.79) * mm});
            skLineSegment(sketch, "E77.2.0.44", {"start": v(-36.76, 10.79) * mm, "end": v(-34.64, 8.66) * mm});
            skLineSegment(sketch, "E77.2.0.45", {"start": v(-19.24, 12.9) * mm, "end": v(-17.12, 10.79) * mm});
            skLineSegment(sketch, "E77.2.0.46", {"start": v(-24.82, 10.79) * mm, "end": v(-26.94, 8.66) * mm});
            skLineSegment(sketch, "E77.2.0.47", {"start": v(11.56, 12.9) * mm, "end": v(9.44, 10.79) * mm});
            skLineSegment(sketch, "E77.2.0.48", {"start": v(-3.84, 12.9) * mm, "end": v(-1.72, 10.79) * mm});
            skLineSegment(sketch, "E77.2.0.49", {"start": v(26.96, 12.9) * mm, "end": v(24.84, 10.79) * mm});
            skLineSegment(sketch, "E77.2.0.50", {"start": v(3.86, 12.9) * mm, "end": v(5.98, 10.79) * mm});
            skLineSegment(sketch, "E77.direction1", {"start": v(-42.3, 20.07) * mm, "end": v(-38.47, 14.37) * mm, "construction": true});
            skPoint(sketch, "E78.0.10.0", {"position": v(34.7, 22.19) * mm});
            skLineSegment(sketch, "E78.1.10.0", {"start": v(36.82, 22.19) * mm, "end": v(34.7, 20.07) * mm});
            skLineSegment(sketch, "E78.4.10.0", {"start": v(34.7, 24.3) * mm, "end": v(36.82, 22.19) * mm});
            skLineSegment(sketch, "E78.7.10.0", {"start": v(34.7, 24.3) * mm, "end": v(32.58, 22.19) * mm});
            skLineSegment(sketch, "E78.10.10.0", {"start": v(32.58, 22.19) * mm, "end": v(34.7, 20.07) * mm});
            skSolve(sketch);
        }
        {
            var Q0;
            Q0=makeQuery(id+"F10.imprint","IMPRINT",FACE,{"disambiguationData":[TD([[makeQuery(id+"F10.imprint","IMPRINT",EDGE,{"derivedFrom":sQuery(id+"F10.wireOp",EDGE,"E74.9.0.1")}),-1.0]])]});
            var Q1;
            Q1=makeQuery(id+"F10.imprint","IMPRINT",FACE,{"disambiguationData":[TD([[makeQuery(id+"F10.imprint","IMPRINT",EDGE,{"derivedFrom":sQuery(id+"F10.wireOp",EDGE,"E74.8.0.1")}),-1.0]])]});
            var Q2;
            Q2=makeQuery(id+"F10.imprint","IMPRINT",FACE,{"disambiguationData":[TD([[makeQuery(id+"F10.imprint","IMPRINT",EDGE,{"derivedFrom":sQuery(id+"F10.wireOp",EDGE,"E77.1.0.2")}),-1.0]])]});
            var Q3;
            Q3=makeQuery(id+"F10.imprint","IMPRINT",FACE,{"disambiguationData":[TD([[makeQuery(id+"F10.imprint","IMPRINT",EDGE,{"derivedFrom":sQuery(id+"F10.wireOp",EDGE,"E77.2.0.10")}),1.0]])]});
            var Q4;
            Q4=makeQuery(id+"F10.imprint","IMPRINT",FACE,{"disambiguationData":[TD([[makeQuery(id+"F10.imprint","IMPRINT",EDGE,{"derivedFrom":sQuery(id+"F10.wireOp",EDGE,"E77.1.0.10")}),1.0]])]});
            var Q5;
            Q5=makeQuery(id+"F10.imprint","IMPRINT",FACE,{"disambiguationData":[TD([[makeQuery(id+"F10.imprint","IMPRINT",EDGE,{"derivedFrom":sQuery(id+"F10.wireOp",EDGE,"E74.7.0.1")}),-1.0]])]});
            var Q6;
            Q6=makeQuery(id+"F10.imprint","IMPRINT",FACE,{"disambiguationData":[TD([[makeQuery(id+"F10.imprint","IMPRINT",EDGE,{"derivedFrom":sQuery(id+"F10.wireOp",EDGE,"E74.6.0.1")}),-1.0]])]});
            var Q7;
            Q7=makeQuery(id+"F10.imprint","IMPRINT",FACE,{"disambiguationData":[TD([[makeQuery(id+"F10.imprint","IMPRINT",EDGE,{"derivedFrom":sQuery(id+"F10.wireOp",EDGE,"E77.1.0.19")}),1.0]])]});
            var Q8;
            Q8=makeQuery(id+"F10.imprint","IMPRINT",FACE,{"disambiguationData":[TD([[makeQuery(id+"F10.imprint","IMPRINT",EDGE,{"derivedFrom":sQuery(id+"F10.wireOp",EDGE,"E77.2.0.19")}),1.0]])]});
            var Q9;
            Q9=makeQuery(id+"F10.imprint","IMPRINT",FACE,{"disambiguationData":[TD([[makeQuery(id+"F10.imprint","IMPRINT",EDGE,{"derivedFrom":sQuery(id+"F10.wireOp",EDGE,"E77.2.0.16")}),1.0]])]});
            var Q10;
            Q10=makeQuery(id+"F10.imprint","IMPRINT",FACE,{"disambiguationData":[TD([[makeQuery(id+"F10.imprint","IMPRINT",EDGE,{"derivedFrom":sQuery(id+"F10.wireOp",EDGE,"E77.1.0.16")}),1.0]])]});
            var Q11;
            Q11=makeQuery(id+"F10.imprint","IMPRINT",FACE,{"disambiguationData":[TD([[makeQuery(id+"F10.imprint","IMPRINT",EDGE,{"derivedFrom":sQuery(id+"F10.wireOp",EDGE,"E74.5.0.1")}),-1.0]])]});
            var Q12;
            Q12=makeQuery(id+"F10.imprint","IMPRINT",FACE,{"disambiguationData":[TD([[makeQuery(id+"F10.imprint","IMPRINT",EDGE,{"derivedFrom":sQuery(id+"F10.wireOp",EDGE,"E74.4.0.1")}),-1.0]])]});
            var Q13;
            Q13=makeQuery(id+"F10.imprint","IMPRINT",FACE,{"disambiguationData":[TD([[makeQuery(id+"F10.imprint","IMPRINT",EDGE,{"derivedFrom":sQuery(id+"F10.wireOp",EDGE,"E77.2.0.1")}),1.0]])]});
            var Q14;
            Q14=makeQuery(id+"F10.imprint","IMPRINT",FACE,{"disambiguationData":[TD([[makeQuery(id+"F10.imprint","IMPRINT",EDGE,{"derivedFrom":sQuery(id+"F10.wireOp",EDGE,"E77.1.0.1")}),1.0]])]});
            var Q15;
            Q15=makeQuery(id+"F10.imprint","IMPRINT",FACE,{"disambiguationData":[TD([[makeQuery(id+"F10.imprint","IMPRINT",EDGE,{"derivedFrom":sQuery(id+"F10.wireOp",EDGE,"E74.3.0.1")}),-1.0]])]});
            var Q16;
            Q16=makeQuery(id+"F10.imprint","IMPRINT",FACE,{"disambiguationData":[TD([[makeQuery(id+"F10.imprint","IMPRINT",EDGE,{"derivedFrom":sQuery(id+"F10.wireOp",EDGE,"E77.1.0.5")}),1.0]])]});
            var Q17;
            Q17=makeQuery(id+"F10.imprint","IMPRINT",FACE,{"disambiguationData":[TD([[makeQuery(id+"F10.imprint","IMPRINT",EDGE,{"derivedFrom":sQuery(id+"F10.wireOp",EDGE,"E77.2.0.5")}),1.0]])]});
            var Q18;
            Q18=makeQuery(id+"F10.imprint","IMPRINT",FACE,{"disambiguationData":[TD([[makeQuery(id+"F10.imprint","IMPRINT",EDGE,{"derivedFrom":sQuery(id+"F10.wireOp",EDGE,"E77.2.0.15")}),1.0]])]});
            var Q19;
            Q19=makeQuery(id+"F10.imprint","IMPRINT",FACE,{"disambiguationData":[TD([[makeQuery(id+"F10.imprint","IMPRINT",EDGE,{"derivedFrom":sQuery(id+"F10.wireOp",EDGE,"E77.1.0.15")}),1.0]])]});
            var Q20;
            Q20=makeQuery(id+"F10.imprint","IMPRINT",FACE,{"disambiguationData":[TD([[makeQuery(id+"F10.imprint","IMPRINT",EDGE,{"derivedFrom":sQuery(id+"F10.wireOp",EDGE,"E74.2.0.1")}),-1.0]])]});
            var Q21;
            Q21=makeQuery(id+"F10.imprint","IMPRINT",FACE,{"disambiguationData":[TD([[makeQuery(id+"F10.imprint","IMPRINT",EDGE,{"derivedFrom":sQuery(id+"F10.wireOp",EDGE,"E74.1.0.1")}),-1.0]])]});
            var Q22;
            Q22=makeQuery(id+"F10.imprint","IMPRINT",FACE,{"disambiguationData":[TD([[makeQuery(id+"F10.imprint","IMPRINT",EDGE,{"derivedFrom":sQuery(id+"F10.wireOp",EDGE,"E77.2.0.28")}),-1.0]])]});
            extrude(context, id + "F11", {"entities" : qUnion([Q0, Q1, Q2, Q3, Q4, Q5, Q6, Q7, Q8, Q9, Q10, Q11, Q12, Q13, Q14, Q15, Q16, Q17, Q18, Q19, Q20, Q21, Q22]), "operationType" : NewBodyOperationType.REMOVE, "oppositeDirection" : true, "depth" : 80 * mm, "offsetDistance" : 25 * mm});
        }
    });
